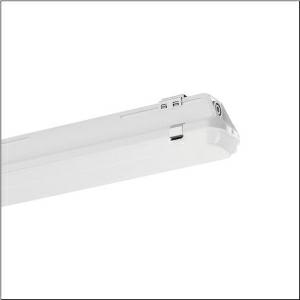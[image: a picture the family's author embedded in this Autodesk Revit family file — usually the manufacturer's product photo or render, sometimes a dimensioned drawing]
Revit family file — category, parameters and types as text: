
# Revit family: monsun_r__12_emergency_51fp10dp460hr_a755
name_source: partatom
category: Lighting Fixtures
units: mm (PartAtom-declared; Revit-internal decimal feet)

## family parameters
Cut with Voids When Loaded = No
Host = Face
Light Source = No
Part Type = Normal
Room Calculation Point = No
Round Connector Dimension = Use Diameter
Shared = No

## types (1)
- --- (1 x LED, 890 lm, 6.9 W, 4000K)
    Apparent Load = 7 VA
    CIE Flux Codes = 47 77 93 94 100
    Color Rendering = 80
    Color Temperature = 4000K
    Default Elevation = 1800 mm
    Description = Monsun® 12 emergency, damp-proof luminaire, chain hanger, primary optical cover: enclosure, of PMMA, light emission: direct distribution, primary light characteristic: symmetric, installation type: suspended mounting, surface-mounted, horizontal mounting, vertical mounting, LED rated luminous flux: 6.050 lm, light colour: 840, colour temperature: 4000K, control gear: ECG DALI, with terminal, 5+2-pole, max. 2.5mm², mains connection: 220..240V, AC/DC, 0/50..60Hz, rated input power: 35W, changeover relay for equivalent power supply, AC/DC, 0/50..60Hz, luminaire housing, of glass-fibre reinforced polyester, uncoated, bright grey, length: 1.590 mm, width: 90 mm, height: 88mm, clip for enclosure, of stainless steel (V2A), ceiling mounting element, of stainless steel (V2A), chain hanger, of stainless steel (V2A), protection rating (complete): IP66, insulation class (complete): insulation class I (protective earthing), certification: CE, protection symbol: D, impact resistance: IK04, permissible ambient temperature for indoor applications: -25..+35°C, standard: EN 50419, EN 60598-2-1, EN 60598-2-22, no direct snow, no direct sun, no direct rain, for indoor or canopied outdoor use, corresponds to IFS (International Featured Standards) requirements for safety and quality in the food industry, packaging unit: 1 piece
    Height = 89 mm
    Lamp = 1 x LED
    Lamp Light Flux = 890 lm
    Lamp Power = 6.9 W
    Lamp count = 1
    Length = 1590 mm
    Luminous efficacy = 129 lm/W
    Manufacturer = Siteco
    ModVariant = No
    Model = 51FP10DP460HR
    Mounting Place = Ceiling
    Mounting Type = Pendant
    Number of Poles = 1
    OnlyDefault = Yes
    Power Factor = 1
    Product Name = Monsun® 12 emergency
    Product group = damp-proof luminaire | ceiling pendant
    ProductGroupID = 908
    Protection Class = Protection class I
    Protection Degree = IP 66
    RLX_Detail_Level = 1
    RlxData = <blob elided: 92177 chars, md5=bc1fb87b>
    Socket = socket
    Standby Power = 0 W
    System Light Flux = 890 lm
    System Power = 7 W
    Type Comments = : equivalent power supply (DC)
    Type Image = l_1004748.jpg
    URL = http://relux.com
    VarID = @adj_125637
    Voltage = 0 V
    Weight = 0.00 kg
    Width = 90 mm

## geometry (parser evidence)
native form markers: Blend x4, Sweep x14
no freeform markers — native parametric forms only
